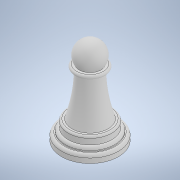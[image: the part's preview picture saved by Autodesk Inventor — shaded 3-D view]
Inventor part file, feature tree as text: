
AUTODESK INVENTOR PART (.ipt)
format: ipt  version: 2022 (Build 260153000, 153)  size: 220,672 bytes
history: native  units: mm
features: other x3, fillet x2, revolve x1, sketch x1, projected_geometry x1
ambient origin geometry x8: Origin, YZ Plane, XZ Plane, XY Plane, X Axis, Y Axis, Z Axis, Center Point
bodies: Solid1 (feature_tree)
feature tree (8):
  other  "Pawn Base.ipt"
  revolve  "Revolution1"  [1 undecoded]
  fillet  "Fillet1"  Radius=2.0mm
  fillet  "Fillet2"  Radius=2.0mm
  other  "Solid1::Pawn Base.ipt"
  other  "TaggingFeature1"
  sketch  "Sketch1"  dims[d0=10.0mm d1=20.0mm d2=2.0mm d3=2.0mm d4=7.0mm d6=4.0mm d8=90.0deg d10=1.0mm d11=1.0mm d12=1.0mm d13=0.5mm d14=0.5mm]
  projected_geometry  "Projected Loop1"
note: 1 required parameter value undecoded (feature->parameter linkage not recoverable at this tier; creation-order binding heuristic only, values carry confidence <= 0.55)
